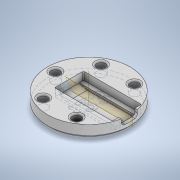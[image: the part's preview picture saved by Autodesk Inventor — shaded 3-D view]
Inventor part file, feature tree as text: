
AUTODESK INVENTOR PART (.ipt)
format: ipt  version: 2021 (Build 250183000, 183)  size: 967,680 bytes
history: native  units: in
note: dims shown in document units (in); Inventor stores cm internally (conversion verified against a paired STEP export)
features: extrude x7, sketch x7, fillet x3, chamfer x2, other x1, plane x1, pattern_circular x1
ambient origin geometry x8: Origin, YZ Plane, XZ Plane, XY Plane, X Axis, Y Axis, Z Axis, Center Point
bodies: Solid1 (feature_tree)
feature tree (22):
  extrude  "Extrusion1"  Depth=0.2992in TaperAngle=0.0deg
  chamfer  "Chamfer2"  Distance=0.1969in
  extrude  "Extrusion2"  Depth=0.1575in
  extrude  "Extrusion3"  Depth=0.2205in
  other  "Work Axis1"
  plane  "Work Plane1"
  extrude  "Extrusion5"  Depth=0.2047in TaperAngle=0.0deg
  extrude  "Extrusion4"  Depth=0.8268in
  fillet  "Fillet4"  Radius=0.3579in
  pattern_circular  "Circular Pattern2"  [2 undecoded]
  chamfer  "Chamfer3"  Distance=1.4in
  fillet  "Fillet7"  Radius=0.25in
  extrude  "Extrusion9"  TaperAngle=0.0deg  [1 undecoded]
  extrude  "Extrusion10"  Depth=0.063in TaperAngle=0.0deg
  fillet  "Fillet9"  Radius=0.1575in
  sketch  "Sketch1"  dims[d0=2.0472in d3=0.2992in d4=0.0in]
  sketch  "Sketch2"  dims[d5=1.4315in]
  sketch  "Sketch3"  dims[d6=0.7157in]
  sketch  "Sketch4"  dims[d7=0.3579in]
  sketch  "Sketch7"  dims[d8=0.4882in d9=0.1969in d10=0.0in]
  sketch  "Sketch12"  dims[d11=0.0in d14=0.1575in]
  sketch  "Sketch13"  dims[d15=0.0in d16=0.0in d17=0.2205in d18=0.2047in d19=0.0in d23=0.8268in d24=0.3579in d28=0.5in d29=1.4in d30=0.25in d31=0.0in d32=0.063in d33=0.0in d44=0.1575in d47=0.0472in d48=0.0in d49=0.0in d51=0.0in d54=0.063in d55=0.0in d56=45.0deg d58=0.0394in d59=0.1181in d60=1.9685in d61=240.0deg d63=0.0591in d64=0.1969in d65=45.0deg d72=0.0315in d79=0.1079in d80=0.9517in d81=0.4759in d82=0.9728in d83=0.4864in d84=0.0157in d85=0.0in d86=0.547in d87=0.2735in d88=0.126in d89=0.0in d90=0.0787in]
note: 3 required parameter values undecoded (feature->parameter linkage not recoverable at this tier; creation-order binding heuristic only, values carry confidence <= 0.55)
